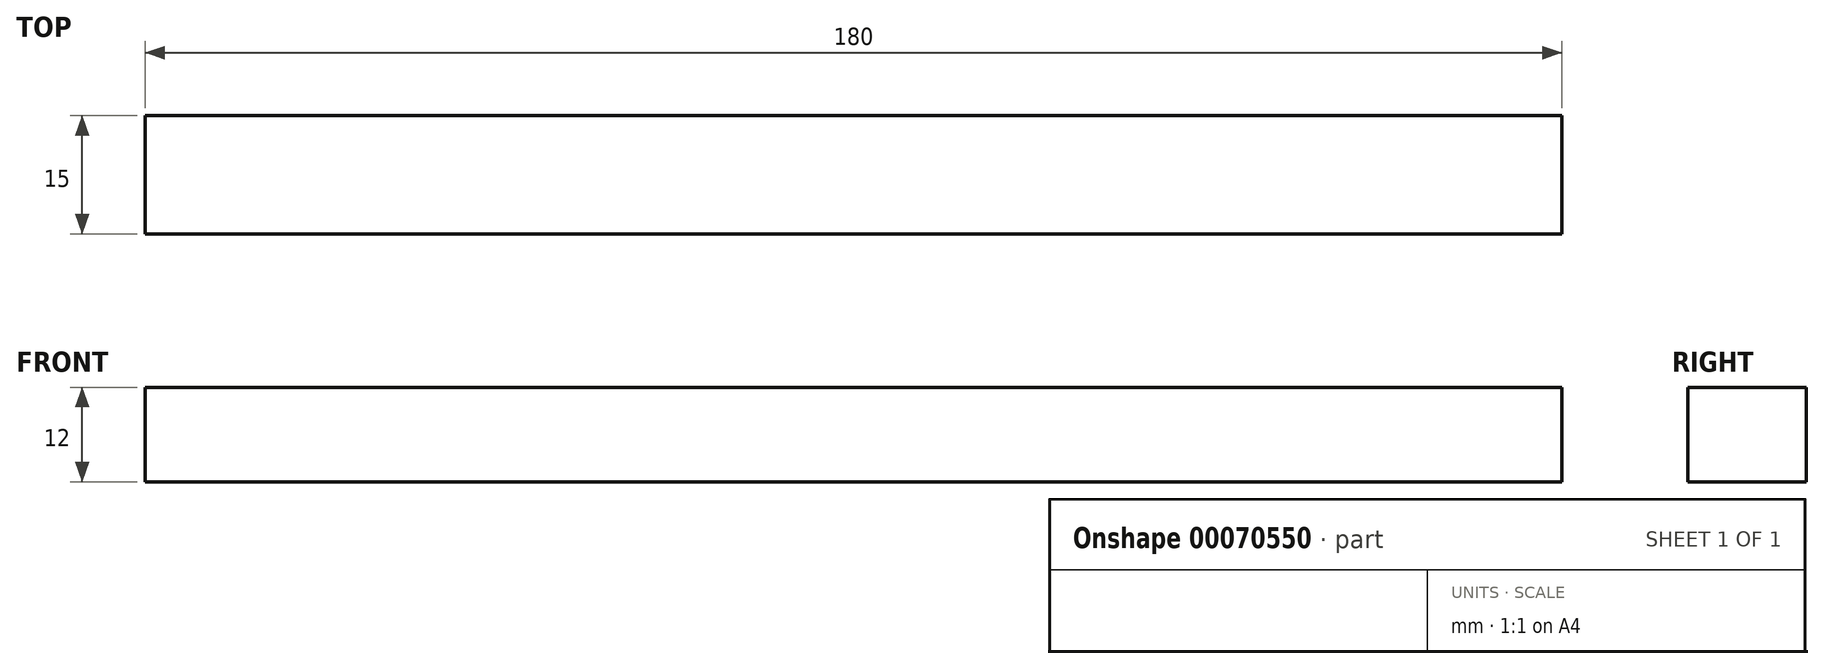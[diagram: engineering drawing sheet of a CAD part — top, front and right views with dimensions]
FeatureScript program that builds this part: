
annotation { "Feature Type Name" : "Feature", "Feature Type Description" : "" }
export const myFeature = defineFeature(function(context is Context, id is Id, definition is map)
    precondition{}
    {
        {
            var Q0;
            Q0=qCreatedBy(makeId("Top.planeOp"),FACE);
            var sketch = newSketch(context, id + "F0", { "sketchPlane" : qUnion([Q0])});
            skLineSegment(sketch, "E0.bottom", {"start": v(0, 0) * mm, "end": v(180, 0) * mm});
            skLineSegment(sketch, "E0.top", {"start": v(0, -15) * mm, "end": v(180, -15) * mm});
            skLineSegment(sketch, "E0.left", {"start": v(0, 0) * mm, "end": v(0, -15) * mm});
            skLineSegment(sketch, "E0.right", {"start": v(180, 0) * mm, "end": v(180, -15) * mm});
            skSolve(sketch);
        }
        {
            var Q0;
            Q0 = qSketchRegion(id + "F0", true);
            extrude(context, id + "F1", {"entities" : qUnion([Q0]), "depth" : 12 * mm});
        }
    });
